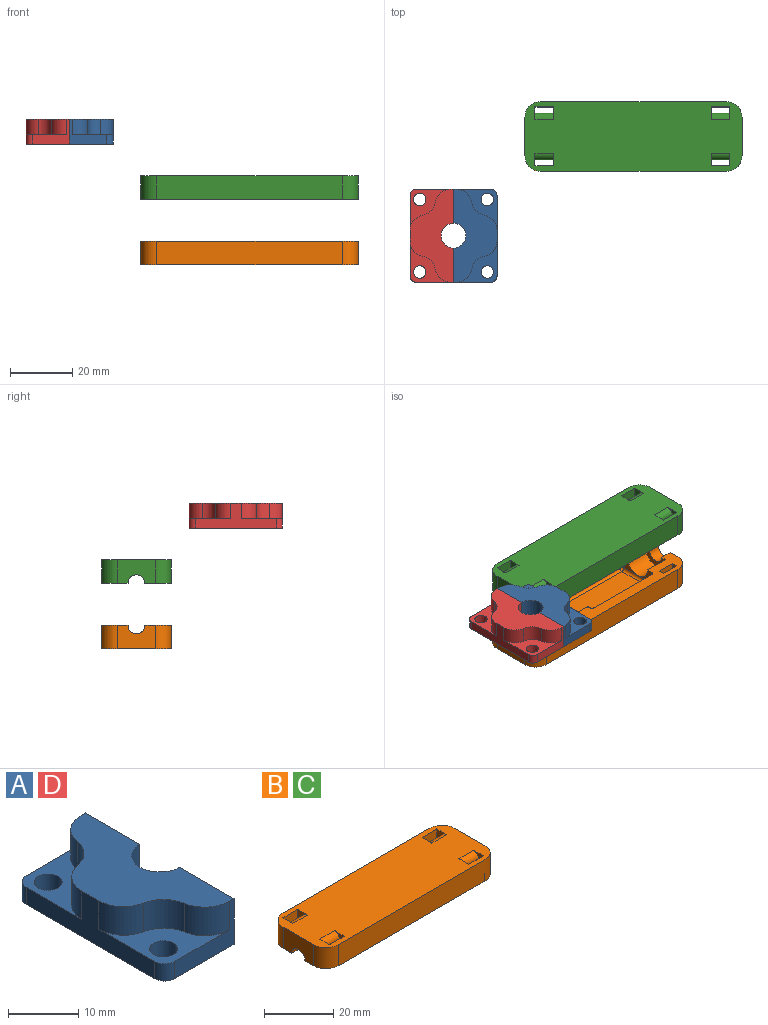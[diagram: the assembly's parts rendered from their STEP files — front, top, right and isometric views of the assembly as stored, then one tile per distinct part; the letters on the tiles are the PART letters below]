
ASSEMBLY  parts=4 mates=2
PART A: 20 faces, bbox 14x30x8 mm
  f0: plane 12x8mm, normal (0,-1,0), area 40.5mm2, adj f1,f8,f9,f13,f14,f19
  f1: plane 11x8mm, normal (1,0,0), area 88mm2, adj f0,f2,f8,f9
  f2: cylinder r=4mm len=8mm, axis (0,0,-1), area 100.5mm2, adj f1,f3,f8,f9
  f3: plane 11x8mm, normal (1,0,0), area 88mm2, adj f2,f4,f8,f9
  f4: plane 12x8mm, normal (0,1,0), area 40.5mm2, adj f3,f8,f9,f11,f15,f16
  f5: cylinder r=5.12mm len=5mm, axis (0,0,-1), area 31.2mm2, adj f8,f11,f16,f17
  f6: plane 26x8mm, normal (-1,0,0), area 95.2mm2, adj f8,f9,f11,f13,f14,f15,f17,f18
  f7: cylinder r=5.12mm len=5mm, axis (0,0,-1), area 31.2mm2, adj f8,f13,f18,f19
  f8: plane 30x14mm, normal (0,0,1), area 247.9mm2, adj f0,f1,f2,f3,f4,f5,f6,f7
  f9: plane 30x14mm, normal (0,0,-1), area 368mm2, adj f0,f1,f2,f3,f4,f6,f10,f12
  f10: cylinder r=2mm len=4mm, axis (0,0,-1), area 37.7mm2, adj f9,f11
  f11: plane 13.28x13.1mm, normal (0,0,1), area 60.1mm2, adj f4,f5,f6,f10,f15,f16,f17
  f12: cylinder r=2mm len=4mm, axis (0,0,-1), area 37.7mm2, adj f9,f13
  f13: plane 13.28x13.1mm, normal (0,0,1), area 60.1mm2, adj f0,f6,f7,f12,f14,f18,f19
  f14: cylinder r=2mm len=3mm, axis (0,0,1), area 9.4mm2, adj f0,f6,f9,f13
  f15: cylinder r=2mm len=3mm, axis (0,0,-1), area 9.4mm2, adj f4,f6,f9,f11
  f16: cylinder r=5mm len=5mm, axis (0,0,-1), area 35.1mm2, adj f4,f5,f8,f11
  f17: cylinder r=5mm len=5mm, axis (0,0,-1), area 34.6mm2, adj f5,f6,f8,f11
  f18: cylinder r=5mm len=5mm, axis (0,0,-1), area 34.6mm2, adj f6,f7,f8,f13
  f19: cylinder r=5mm len=5mm, axis (0,0,-1), area 35.1mm2, adj f0,f7,f8,f13
PART B: 76 faces, bbox 69.9x22.4x7.5 mm
  f0: plane 69.85x8.51mm, normal (0,0,-1), area 361.9mm2, adj f4,f5,f6,f8,f9,f12,f13,f15
  f1: plane 69.85x8.51mm, normal (0,0,-1), area 361.9mm2, adj f3,f4,f6,f7,f10,f11,f14,f16
  f2: plane 69.85x22.41mm, normal (0,0,1), area 1447.9mm2, adj f3,f4,f5,f6,f7,f8,f9,f10
  f3: plane 59.85x7.5mm, normal (0,1,0), area 448.9mm2, adj f1,f2,f7,f10
  f4: plane 12.41x7.5mm, normal (-1,0,0), area 81.6mm2, adj f0,f1,f2,f7,f8,f30
  f5: plane 59.85x7.5mm, normal (0,-1,0), area 448.9mm2, adj f0,f2,f8,f9
  f6: plane 12.41x7.5mm, normal (1,0,0), area 81.6mm2, adj f0,f1,f2,f9,f10,f20
  f7: cylinder r=5mm len=7.5mm, axis (0,0,1), area 58.9mm2, adj f1,f2,f3,f4
  f8: cylinder r=5mm len=7.5mm, axis (0,0,-1), area 58.9mm2, adj f0,f2,f4,f5
  f9: cylinder r=5mm len=7.5mm, axis (0,0,1), area 58.9mm2, adj f0,f2,f5,f6
  f10: cylinder r=5mm len=7.5mm, axis (0,0,-1), area 58.9mm2, adj f1,f2,f3,f6
  f11: plane 4.5x1.39mm, normal (1,0,0), area 1.9mm2, adj f1,f23,f33,f41,f49
  f12: plane 4.5x1.39mm, normal (1,0,0), area 1.9mm2, adj f0,f24,f31,f41,f46
  f13: plane 3.5x0.99mm, normal (1,0,0), area 2.6mm2, adj f0,f28,f32,f52,f54
  f14: plane 3.5x0.99mm, normal (1,0,0), area 2.6mm2, adj f1,f29,f34,f52,f55
  f15: plane 26x4.5mm, normal (0,1,0), area 117mm2, adj f0,f22,f24,f42
  f16: plane 12.41x4.5mm, normal (-1,0,0), area 24.3mm2, adj f0,f1,f19,f21,f22,f38
  f17: plane 26x4.5mm, normal (0,-1,0), area 117mm2, adj f1,f21,f23,f37
  f18: plane 8.96x4.48mm, normal (-1,0,0), area 20.1mm2, adj f0,f1,f19,f20
  f19: cylinder r=4.48mm len=8.96mm, axis (1,0,0), area 113.9mm2, adj f0,f1,f16,f18
  f20: cylinder r=2.7mm len=5.4mm, axis (1,0,0), area 33.9mm2, adj f0,f1,f6,f18
  f21: cylinder r=1mm len=4.5mm, axis (0,0,1), area 7.1mm2, adj f1,f16,f17,f36
  f22: cylinder r=1mm len=4.5mm, axis (0,0,-1), area 7.1mm2, adj f0,f15,f16,f40
  f23: cylinder r=1mm len=4.5mm, axis (0,0,1), area 7.1mm2, adj f1,f11,f17,f39
  f24: cylinder r=1mm len=4.5mm, axis (0,0,-1), area 7.1mm2, adj f0,f12,f15,f43
  f25: plane 16.6x3.5mm, normal (0,-1,0), area 58.1mm2, adj f1,f33,f34,f51
  f26: plane 16.6x3.5mm, normal (0,1,0), area 58.1mm2, adj f0,f31,f32,f48
  f27: plane 8.16x3.5mm, normal (1,0,0), area 17.1mm2, adj f0,f1,f28,f29,f30,f45,f54,f55
  f28: plane 8.16x3.25mm, normal (0,1,0), area 26.5mm2, adj f0,f13,f27,f54
  f29: plane 8.16x3.25mm, normal (0,-1,0), area 26.5mm2, adj f1,f14,f27,f55
  f30: cylinder r=2.7mm len=5.4mm, axis (-1,0,0), area 33.9mm2, adj f0,f1,f4,f27
  f31: cylinder r=0.5mm len=3.5mm, axis (0,0,1), area 2.7mm2, adj f0,f12,f26,f46
  f32: cylinder r=0.5mm len=3.5mm, axis (0,0,-1), area 2.7mm2, adj f0,f13,f26,f50
  f33: cylinder r=0.5mm len=3.5mm, axis (0,0,-1), area 2.7mm2, adj f1,f11,f25,f49
  f34: cylinder r=0.5mm len=3.5mm, axis (0,0,1), area 2.7mm2, adj f1,f14,f25,f53
  f35: plane 26x12.41mm, normal (0,0,-1), area 322.7mm2, adj f37,f38,f41,f42
  f36: sphere r=1mm, area 1.6mm2, adj f21,f37,f38
  f37: cylinder r=1mm len=26mm, axis (1,0,0), area 40.8mm2, adj f17,f35,f36,f39
  f38: cylinder r=1mm len=12.41mm, axis (0,-1,0), area 19.5mm2, adj f16,f35,f36,f40
  f39: sphere r=1mm, area 1.6mm2, adj f23,f37,f41
  f40: sphere r=1mm, area 1.6mm2, adj f22,f38,f42
  f41: cylinder r=1mm len=12.41mm, axis (0,1,0), area 19.5mm2, adj f11,f12,f35,f39,f43,f47
  f42: cylinder r=1mm len=26mm, axis (-1,0,0), area 40.8mm2, adj f15,f35,f40,f43
  f43: sphere r=1mm, area 1.6mm2, adj f24,f41,f42
  f44: plane 16.6x9.64mm, normal (0,0,-1), area 160mm2, adj f47,f48,f51,f52
  f45: plane 8.16x7.66mm, normal (0,0,-1), area 62.5mm2, adj f27,f52,f54,f55
  f46: torus R=1mm, axis (1,0,0), area 0.8mm2, adj f12,f31,f47,f48
  f47: cylinder r=0.5mm len=9.64mm, axis (0,-1,0), area 7.6mm2, adj f41,f44,f46,f49
  f48: cylinder r=0.5mm len=16.6mm, axis (-1,0,0), area 13mm2, adj f26,f44,f46,f50
  f49: torus R=1mm, axis (1,0,0), area 0.8mm2, adj f11,f33,f47,f51
  f50: sphere r=0.5mm, area 0.4mm2, adj f32,f48,f52
  f51: cylinder r=0.5mm len=16.6mm, axis (1,0,0), area 13mm2, adj f25,f44,f49,f53
  f52: cylinder r=0.5mm len=9.64mm, axis (0,1,0), area 7.6mm2, adj f13,f14,f44,f45,f50,f53
  f53: sphere r=0.5mm, area 0.4mm2, adj f34,f51,f52
  f54: cylinder r=0.25mm len=8.16mm, axis (-1,0,0), area 3.2mm2, adj f13,f27,f28,f45
  f55: cylinder r=0.25mm len=8.16mm, axis (1,0,0), area 3.2mm2, adj f14,f27,f29,f45
  f56: plane 6x5.5mm, normal (0,1,0), area 33mm2, adj f1,f57,f59,f75
  f57: plane 7.5x4mm, normal (1,0,0), area 15.9mm2, adj f1,f2,f56,f58,f75
  f58: plane 7.5x6mm, normal (0,-1,0), area 45mm2, adj f1,f2,f57,f59
  f59: plane 7.5x4mm, normal (-1,0,0), area 15.9mm2, adj f1,f2,f56,f58,f75
  f60: plane 7.5x4mm, normal (-1,0,0), area 15.9mm2, adj f0,f2,f61,f63,f74
  f61: plane 7.5x6mm, normal (0,1,0), area 45mm2, adj f0,f2,f60,f62
  f62: plane 7.5x4mm, normal (1,0,0), area 15.9mm2, adj f0,f2,f61,f63,f74
  f63: plane 6x5.5mm, normal (0,-1,0), area 33mm2, adj f0,f60,f62,f74
  f64: plane 7.5x6mm, normal (0,1,0), area 45mm2, adj f0,f2,f65,f67
  f65: plane 7.5x4mm, normal (1,0,0), area 15.9mm2, adj f0,f2,f64,f66,f73
  f66: plane 6x5.5mm, normal (0,-1,0), area 33mm2, adj f0,f65,f67,f73
  f67: plane 7.5x4mm, normal (-1,0,0), area 15.9mm2, adj f0,f2,f64,f66,f73
  f68: plane 7.5x4mm, normal (-1,0,0), area 15.9mm2, adj f1,f2,f69,f71,f72
  f69: plane 6x5.5mm, normal (0,1,0), area 33mm2, adj f1,f68,f70,f72
  f70: plane 7.5x4mm, normal (1,0,0), area 15.9mm2, adj f1,f2,f69,f71,f72
  f71: plane 7.5x6mm, normal (0,-1,0), area 45mm2, adj f1,f2,f68,f70
  f72: cylinder r=2mm len=6mm, axis (-1,0,0), area 18.8mm2, adj f2,f68,f69,f70
  f73: cylinder r=2mm len=6mm, axis (1,0,0), area 18.8mm2, adj f2,f65,f66,f67
  f74: cylinder r=2mm len=6mm, axis (1,0,0), area 18.8mm2, adj f2,f60,f62,f63
  f75: cylinder r=2mm len=6mm, axis (-1,0,0), area 18.8mm2, adj f2,f56,f57,f59
PART C: same geometry as B
PART D: same geometry as A
PLACE A rot(axis=(0,0,1),180deg) t=(6.57,-0.35,-2.33)mm
PLACE B rot(axis=(1,0,0),180deg) t=(68.63,31.64,-33.67)mm fixed
PLACE C t=(68.63,31.64,-20.06)mm
PLACE D t=(6.57,-0.35,-2.33)mm
MATE slider B.f1 <-> C.f0  axis (0,0,1) through (35.78,23.14,-33.67)mm
MATE fastened A.f1 <-> D.f3  axis (-1,0,0) through (6.57,9.15,1.67)mm
